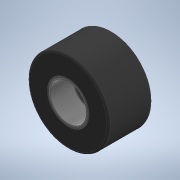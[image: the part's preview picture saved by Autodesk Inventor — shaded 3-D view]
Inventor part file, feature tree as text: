
AUTODESK INVENTOR PART (.ipt)
format: ipt  version: 2022 (Build 260153000, 153)  size: 371,712 bytes
history: native  units: in
note: dims shown in document units (in); Inventor stores cm internally (conversion verified against a paired STEP export)
features: fillet x3, sketch x3, extrude x2, revolve x1
ambient origin geometry x8: Origin, YZ Plane, XZ Plane, XY Plane, X Axis, Y Axis, Z Axis, Center Point
bodies: Solid1 (feature_tree)
feature tree (9):
  revolve  "Revolution1"  [1 undecoded]
  fillet  "Fillet1"  Radius=0.6875in
  fillet  "Fillet2"  Radius=0.0625in
  extrude  "Extrusion1"  Depth=0.125in
  extrude  "Extrusion2"  Depth=0.1875in
  fillet  "Fillet3"  Radius=0.125in
  sketch  "Sketch1"  dims[d0=1.4in d1=1.5in d2=0.6875in d3=0.0625in]
  sketch  "Sketch2"  dims[d4=0.3125in d5=0.5625in d6=0.125in]
  sketch  "Sketch3"  dims[d7=0.275in d9=0.1875in d11=0.125in d12=360.0deg d13=0.0197in d14=0.0039in d15=0.0197in d16=0.0039in d17=0.0312in d18=0.0625in d19=0.625in d20=0.325in d21=0.64in d22=0.15in d23=0.25in d24=0.7874in d26=360.0deg d28=1.0in d29=0.0in d30=0.625in d31=0.138in d32=0.7874in d34=360.0deg d36=0.0in d37=0.0in d38=0.0197in d39=0.125in]
note: 1 required parameter value undecoded (feature->parameter linkage not recoverable at this tier; creation-order binding heuristic only, values carry confidence <= 0.55)
